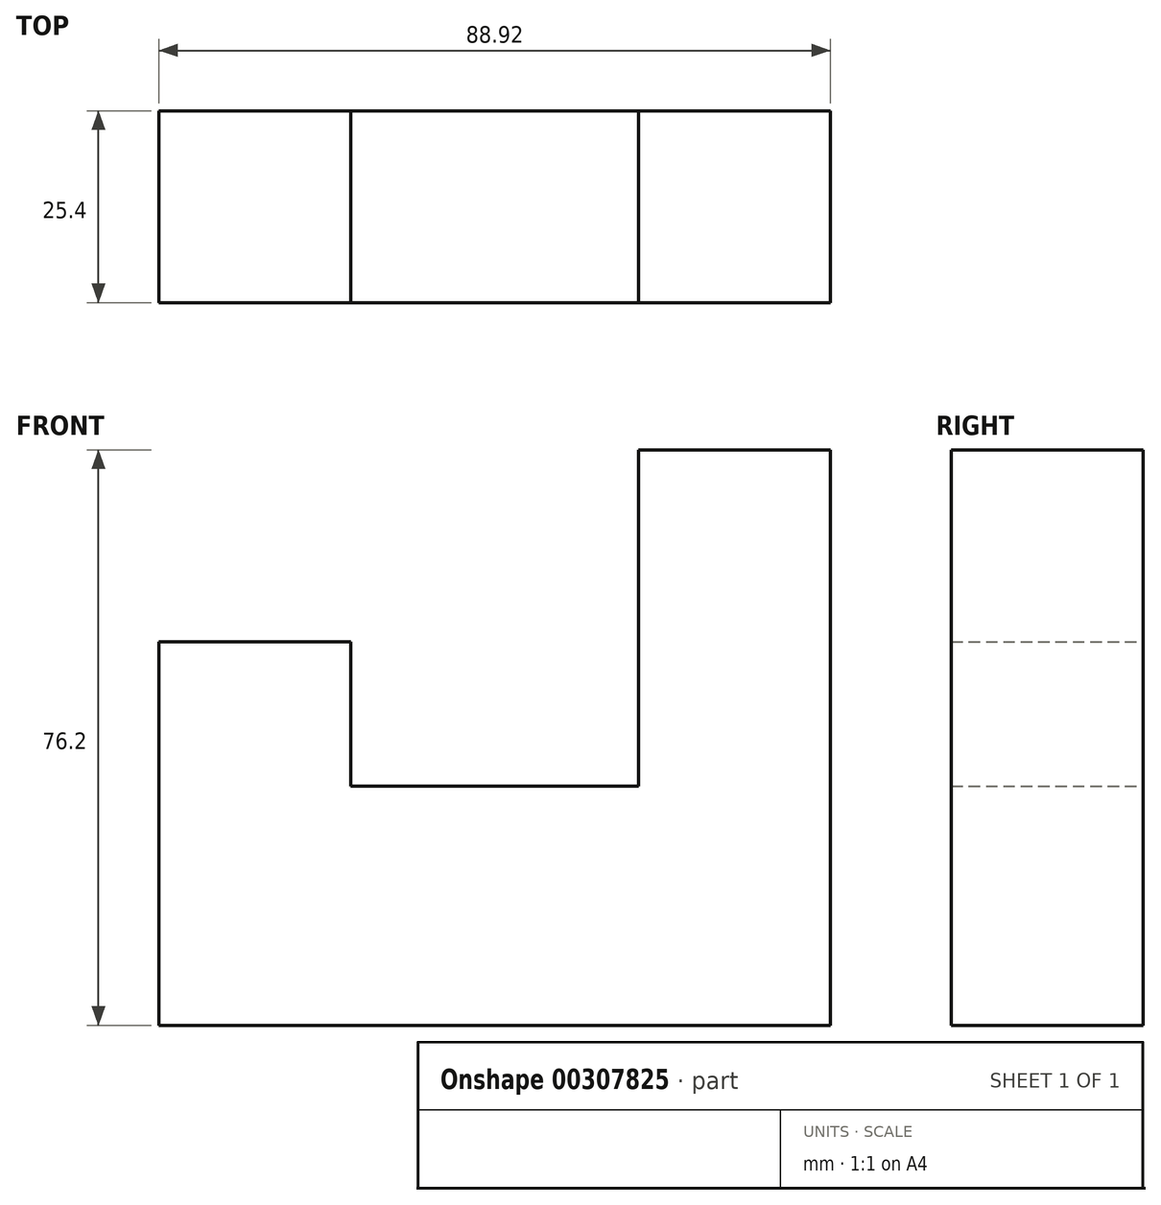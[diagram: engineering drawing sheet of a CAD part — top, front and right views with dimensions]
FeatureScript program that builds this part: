
annotation { "Feature Type Name" : "Feature", "Feature Type Description" : "" }
export const myFeature = defineFeature(function(context is Context, id is Id, definition is map)
    precondition{}
    {
        {
            var Q0;
            Q0=qCreatedBy(makeId("Front.planeOp"),FACE);
            var sketch = newSketch(context, id + "F0", { "sketchPlane" : qUnion([Q0])});
            skLineSegment(sketch, "E0", {"start": v(-50.82, -15.6) * mm, "end": v(-25.41, -15.6) * mm});
            skLineSegment(sketch, "E1", {"start": v(-25.41, -15.6) * mm, "end": v(-25.41, -34.76) * mm});
            skLineSegment(sketch, "E2", {"start": v(-25.41, -34.76) * mm, "end": v(12.69, -34.76) * mm});
            skLineSegment(sketch, "E3", {"start": v(12.69, -34.76) * mm, "end": v(12.69, 9.8) * mm});
            skLineSegment(sketch, "E4", {"start": v(12.69, 9.8) * mm, "end": v(38.1, 9.8) * mm});
            skLineSegment(sketch, "E5", {"start": v(38.1, 9.8) * mm, "end": v(38.1, -28.3) * mm});
            skLineSegment(sketch, "E6", {"start": v(38.1, -28.3) * mm, "end": v(38.1, -66.4) * mm});
            skLineSegment(sketch, "E7", {"start": v(38.1, -66.4) * mm, "end": v(-50.8, -66.4) * mm});
            skLineSegment(sketch, "E8", {"start": v(-50.8, -66.4) * mm, "end": v(-50.82, -66.4) * mm});
            skLineSegment(sketch, "E9", {"start": v(-50.82, -66.4) * mm, "end": v(-50.82, -15.6) * mm});
            skSolve(sketch);
        }
        {
            var Q0;
            Q0=makeQuery(id+"F0.imprint","IMPRINT",FACE,{"disambiguationData":[TD([[makeQuery(id+"F0.imprint","IMPRINT",EDGE,{"derivedFrom":sQuery(id+"F0.wireOp",EDGE,"E0")}),-1.0]])]});
            extrude(context, id + "F1", {"entities" : qUnion([Q0]), "depth" : 25.4 * mm});
        }
    });
